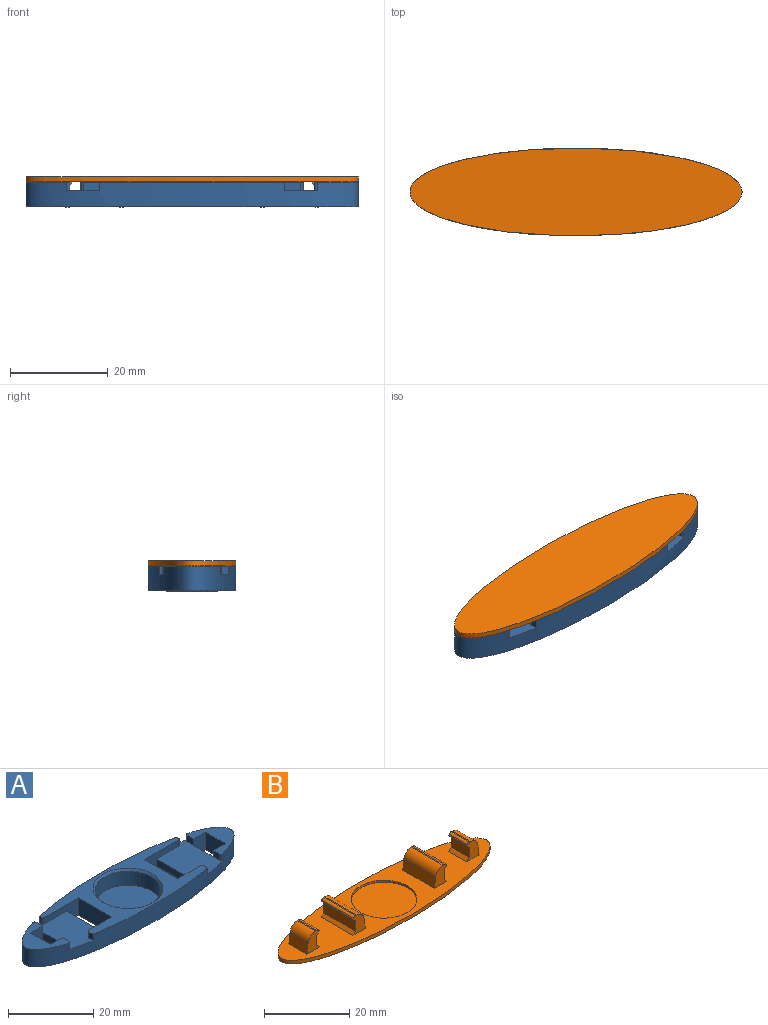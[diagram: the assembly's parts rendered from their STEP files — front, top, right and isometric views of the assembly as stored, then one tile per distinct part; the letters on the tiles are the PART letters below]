
ASSEMBLY  parts=2 mates=1
PART A: 46 faces, bbox 68x18x5 mm
  f0: plane 6.5x2mm, normal (1,0,0), area 13mm2, adj f17,f19,f25,f42
  f1: plane 6.5x2mm, normal (-1,0,0), area 13mm2, adj f20,f21,f30,f45
  f2: plane 45.6x18mm, normal (0,0,1), area 271.1mm2, adj f5,f9,f10,f12,f14,f15,f16,f26
  f3: plane 11.86x9mm, normal (0,0,1), area 49.2mm2, adj f5,f17,f18,f19,f23,f24,f36,f37
  f4: plane 11.86x9mm, normal (0,0,1), area 49.2mm2, adj f5,f20,f21,f22,f28,f29,f34,f35
  f5: extruded ~68x18mm, area 699.2mm2, adj f2,f3,f4,f6,f25,f26,f27,f30
  f6: plane 68x18mm, normal (0,0,-1), area 779.3mm2, adj f5,f9,f10,f12,f14,f15,f16,f17
  f7: cylinder r=7.7mm len=15.4mm, axis (0,0,1), area 198.4mm2, adj f8,f33
  f8: plane 15.4x15.4mm, normal (0,0,1), area 186.3mm2, adj f7
  f9: plane 11x5mm, normal (-1,0,0), area 55mm2, adj f2,f6,f10,f12
  f10: plane 11.3x5mm, normal (0,-1,0), area 33.9mm2, adj f2,f6,f9,f11,f30,f41,f44
  f11: plane 11x2mm, normal (1,0,0), area 22mm2, adj f10,f12,f30,f44
  f12: plane 7.5x5mm, normal (0,1,0), area 27mm2, adj f2,f6,f9,f11,f30,f40,f44
  f13: plane 11x2mm, normal (-1,0,0), area 22mm2, adj f14,f16,f25,f43
  f14: plane 11.3x5mm, normal (0,-1,0), area 33.9mm2, adj f2,f6,f13,f15,f25,f38,f43
  f15: plane 11x5mm, normal (1,0,0), area 55mm2, adj f2,f6,f14,f16
  f16: plane 7.5x5mm, normal (0,1,0), area 27mm2, adj f2,f6,f13,f15,f25,f39,f43
  f17: plane 5.2x5mm, normal (0,1,0), area 20.7mm2, adj f0,f3,f6,f18,f24,f42
  f18: plane 6.5x5mm, normal (-1,0,0), area 32.5mm2, adj f3,f6,f17,f19
  f19: plane 5.2x5mm, normal (0,-1,0), area 20.7mm2, adj f0,f3,f6,f18,f23,f42
  f20: plane 5.2x5mm, normal (0,1,0), area 20.7mm2, adj f1,f4,f6,f22,f29,f45
  f21: plane 5.2x5mm, normal (0,-1,0), area 20.7mm2, adj f1,f4,f6,f22,f28,f45
  f22: plane 6.5x5mm, normal (1,0,0), area 32.5mm2, adj f4,f6,f20,f21
  f23: plane 2.18x1.8mm, normal (-1,0,0), area 3.9mm2, adj f3,f19,f25,f36
  f24: plane 2.18x1.8mm, normal (-1,0,0), area 3.9mm2, adj f3,f17,f25,f37
  f25: plane 14.14x10.65mm, normal (0,0,1), area 120.3mm2, adj f0,f5,f13,f14,f16,f23,f24,f26
  f26: plane 1.8x0.68mm, normal (1,0,0), area 1.2mm2, adj f2,f5,f25,f38
  f27: plane 1.8x1.46mm, normal (1,0,0), area 2.6mm2, adj f2,f5,f25,f39
  f28: plane 2.18x1.8mm, normal (1,0,0), area 3.9mm2, adj f4,f21,f30,f34
  f29: plane 2.18x1.8mm, normal (1,0,0), area 3.9mm2, adj f4,f20,f30,f35
  f30: plane 14.14x10.65mm, normal (0,0,1), area 120.3mm2, adj f1,f5,f10,f11,f12,f28,f29,f31
  f31: plane 1.8x1.46mm, normal (-1,0,0), area 2.6mm2, adj f2,f5,f30,f40
  f32: plane 1.8x0.68mm, normal (-1,0,0), area 1.2mm2, adj f2,f5,f30,f41
  f33: cone r=7.7mm half-angle=45deg, axis (0,0,1), area 35.3mm2, adj f2,f7
  f34: cylinder r=0.5mm len=1.8mm, axis (0,0,-1), area 1.7mm2, adj f4,f5,f28,f30
  f35: cylinder r=0.5mm len=1.8mm, axis (0,0,-1), area 1.7mm2, adj f4,f5,f29,f30
  f36: cylinder r=0.5mm len=1.8mm, axis (0,0,-1), area 1.7mm2, adj f3,f5,f23,f25
  f37: cylinder r=0.5mm len=1.8mm, axis (0,0,-1), area 1.7mm2, adj f3,f5,f24,f25
  f38: cylinder r=0.5mm len=1.8mm, axis (0,0,1), area 1.4mm2, adj f2,f14,f25,f26
  f39: cylinder r=0.5mm len=1.8mm, axis (0,0,1), area 1.4mm2, adj f2,f16,f25,f27
  f40: cylinder r=0.5mm len=1.8mm, axis (0,0,1), area 1.4mm2, adj f2,f12,f30,f31
  f41: cylinder r=0.5mm len=1.8mm, axis (0,0,1), area 1.4mm2, adj f2,f10,f30,f32
  f42: plane 6.5x1.2mm, normal (0.71,0,-0.71), area 11mm2, adj f0,f6,f17,f19
  f43: plane 11x1.2mm, normal (-0.71,0,-0.71), area 18.7mm2, adj f6,f13,f14,f16
  f44: plane 11x1.2mm, normal (0.71,0,-0.71), area 18.7mm2, adj f6,f10,f11,f12
  f45: plane 6.5x1.2mm, normal (-0.71,0,-0.71), area 11mm2, adj f1,f6,f20,f21
PART B: 47 faces, bbox 68x18x6.2 mm
  f0: plane 5.2x4.1mm, normal (0,1,0), area 15.4mm2, adj f2,f8,f10,f21,f28,f31,f34,f37
  f1: plane 5.2x4.1mm, normal (0,-1,0), area 15.4mm2, adj f2,f8,f10,f21,f28,f31,f34,f37
  f2: plane 10.5x0.33mm, normal (0,0,1), area 3.5mm2, adj f0,f1,f40,f43
  f3: plane 5.2x4.1mm, normal (0,1,0), area 15.4mm2, adj f5,f7,f10,f20,f25,f32,f33,f35
  f4: plane 5.2x4.1mm, normal (0,-1,0), area 15.4mm2, adj f5,f7,f10,f20,f25,f32,f33,f35
  f5: plane 6x0.33mm, normal (0,0,1), area 2mm2, adj f3,f4,f42,f44
  f6: plane 5.2x4.1mm, normal (0,-1,0), area 15.4mm2, adj f10,f18,f19,f23,f26,f30,f36,f41
  f7: plane 6x0.8mm, normal (-0.71,0,-0.71), area 6.8mm2, adj f3,f4,f20,f32
  f8: plane 10.5x0.8mm, normal (-0.71,0,-0.71), area 11.9mm2, adj f0,f1,f21,f31
  f9: plane 5.2x4.1mm, normal (0,1,0), area 15.4mm2, adj f10,f18,f19,f23,f26,f30,f36,f41
  f10: plane 68x18mm, normal (0,0,1), area 639.8mm2, adj f0,f1,f3,f4,f6,f9,f11,f13
  f11: extruded ~68x18mm, area 146.9mm2, adj f10,f12
  f12: plane 68x18mm, normal (0,0,-1), area 961.3mm2, adj f11
  f13: cylinder r=7.7mm len=15.4mm, axis (0,0,1), area 29mm2, adj f10,f14
  f14: plane 15.4x15.4mm, normal (0,0,1), area 186.3mm2, adj f13
  f15: plane 5.2x4.1mm, normal (0,1,0), area 15.4mm2, adj f10,f17,f22,f24,f27,f29,f38,f39
  f16: plane 5.2x4.1mm, normal (0,-1,0), area 15.4mm2, adj f10,f17,f22,f24,f27,f29,f38,f39
  f17: plane 6x0.35mm, normal (0,0,1), area 2.1mm2, adj f15,f16,f39,f45
  f18: plane 10.5x0.35mm, normal (0,0,1), area 3.7mm2, adj f6,f9,f41,f46
  f19: plane 10.5x3mm, normal (1,0,0), area 31.5mm2, adj f6,f9,f23,f26
  f20: plane 6x3mm, normal (-1,0,0), area 18mm2, adj f3,f4,f7,f25
  f21: plane 10.5x3mm, normal (-1,0,0), area 31.5mm2, adj f0,f1,f8,f28
  f22: plane 6x3mm, normal (1,0,0), area 18mm2, adj f15,f16,f24,f27
  f23: plane 10.5x0.8mm, normal (0.71,0,-0.71), area 11.9mm2, adj f6,f9,f19,f30
  f24: plane 6x0.8mm, normal (0.71,0,-0.71), area 6.8mm2, adj f15,f16,f22,f29
  f25: plane 6x0.8mm, normal (-0.71,0,0.71), area 6.8mm2, adj f3,f4,f10,f20
  f26: plane 10.5x0.8mm, normal (0.71,0,0.71), area 11.9mm2, adj f6,f9,f10,f19
  f27: plane 6x0.8mm, normal (0.71,0,0.71), area 6.8mm2, adj f10,f15,f16,f22
  f28: plane 10.5x0.8mm, normal (-0.71,0,0.71), area 11.9mm2, adj f0,f1,f10,f21
  f29: plane 6x0.1mm, normal (1,0,0), area 0.6mm2, adj f15,f16,f24,f45
  f30: plane 10.5x0.1mm, normal (1,0,0), area 1.1mm2, adj f6,f9,f23,f46
  f31: plane 10.5x0.1mm, normal (-1,0,0), area 1.1mm2, adj f0,f1,f8,f34
  f32: plane 6x0.1mm, normal (-1,0,0), area 0.6mm2, adj f3,f4,f7,f33
  f33: plane 6x0.14mm, normal (-0.77,0,0.64), area 1.1mm2, adj f3,f4,f32,f44
  f34: plane 10.5x0.14mm, normal (-0.77,0,0.64), area 2mm2, adj f0,f1,f31,f43
  f35: plane 6x3.03mm, normal (0.99,0,0.13), area 18.3mm2, adj f3,f4,f10,f42
  f36: plane 10.5x3.03mm, normal (-0.99,0,0.13), area 32.1mm2, adj f6,f9,f10,f41
  f37: plane 10.5x3.03mm, normal (0.99,0,0.13), area 32.1mm2, adj f0,f1,f10,f40
  f38: plane 6x3.03mm, normal (-0.99,0,0.13), area 18.3mm2, adj f10,f15,f16,f39
  f39: cylinder r=2.5mm len=6mm, axis (0,1,0), area 21.6mm2, adj f15,f16,f17,f38
  f40: cylinder r=2.5mm len=10.5mm, axis (0,1,0), area 37.8mm2, adj f0,f1,f2,f37
  f41: cylinder r=2.5mm len=10.5mm, axis (0,1,0), area 37.8mm2, adj f6,f9,f18,f36
  f42: cylinder r=2.5mm len=6mm, axis (0,1,0), area 21.6mm2, adj f3,f4,f5,f35
  f43: cylinder r=1mm len=10.5mm, axis (0,1,0), area 9.2mm2, adj f0,f1,f2,f34
  f44: cylinder r=1mm len=6mm, axis (0,1,0), area 5.2mm2, adj f3,f4,f5,f33
  f45: cylinder r=1mm len=6mm, axis (0,1,0), area 6.3mm2, adj f15,f16,f17,f29
  f46: cylinder r=1mm len=10.5mm, axis (0,1,0), area 11mm2, adj f6,f9,f18,f30
PLACE A t=(0.22,0.15,-2.27)mm fixed
PLACE B rot(axis=(1,0,0),180deg) t=(0.22,0.15,3.81)mm
MATE slider B.f13 <-> A.f7  axis (0,0,-1) through (0.22,0.15,3.41)mm
